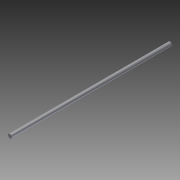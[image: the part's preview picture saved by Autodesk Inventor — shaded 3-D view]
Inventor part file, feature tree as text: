
AUTODESK INVENTOR PART (.ipt)
format: ipt  version: 2012 (Build 160160000, 160)  size: 62,976 bytes
history: native  units: in
note: dims shown in document units (in); Inventor stores cm internally (conversion verified against a paired STEP export)
features: extrude x1, sketch x1
ambient origin geometry x8: Origin, YZ Plane, XZ Plane, XY Plane, X Axis, Y Axis, Z Axis, Center Point
bodies: Solid1 (feature_tree)
feature tree (2):
  extrude  "Extrusion1"  Depth=20.25in TaperAngle=0.0deg
  sketch  "Sketch1"  dims[d0=0.5in d1=20.25in d2=0.0in]
